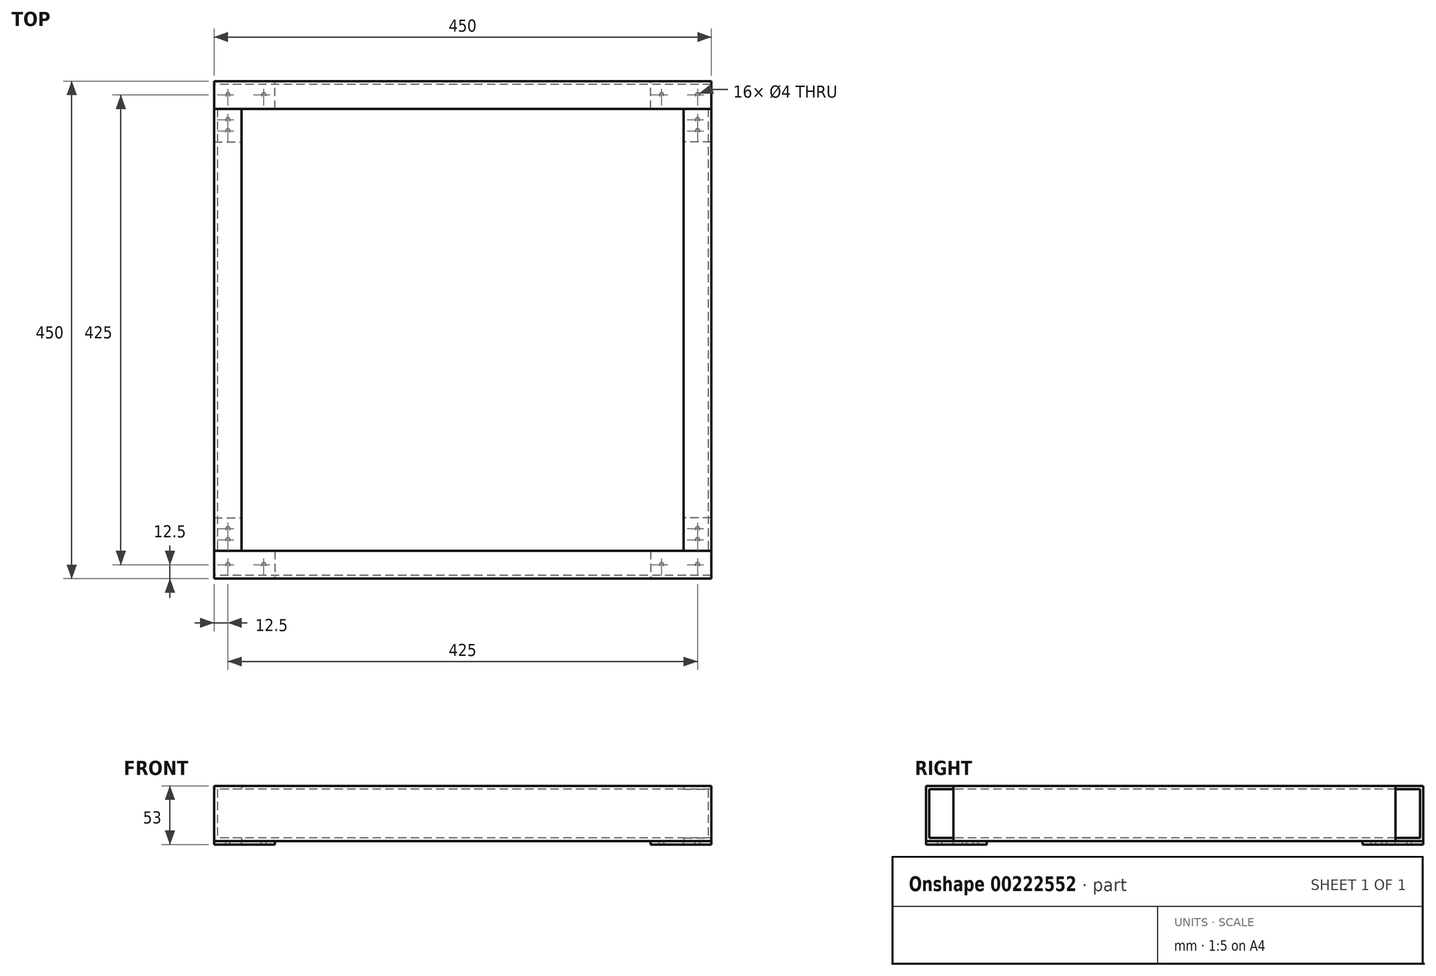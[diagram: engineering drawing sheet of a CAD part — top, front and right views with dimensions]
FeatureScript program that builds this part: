
annotation { "Feature Type Name" : "Feature", "Feature Type Description" : "" }
export const myFeature = defineFeature(function(context is Context, id is Id, definition is map)
    precondition{}
    {
        {
            var Q0;
            Q0=qCreatedBy(makeId("Top.planeOp"),FACE);
            var sketch = newSketch(context, id + "F0", { "sketchPlane" : qUnion([Q0])});
            skLineSegment(sketch, "E0.bottom", {"start": v(225, -225) * mm, "end": v(-225, -225) * mm});
            skLineSegment(sketch, "E0.top", {"start": v(225, 225) * mm, "end": v(-225, 225) * mm});
            skLineSegment(sketch, "E0.left", {"start": v(225, -225) * mm, "end": v(225, 225) * mm});
            skLineSegment(sketch, "E0.right", {"start": v(-225, -225) * mm, "end": v(-225, 225) * mm});
            skPoint(sketch, "E0.middle", {"position": v(0, 0) * mm});
            skLineSegment(sketch, "E1.bottom", {"start": v(200, -200) * mm, "end": v(-200, -200) * mm});
            skLineSegment(sketch, "E1.top", {"start": v(200, 200) * mm, "end": v(-200, 200) * mm});
            skLineSegment(sketch, "E1.left", {"start": v(200, -200) * mm, "end": v(200, 200) * mm});
            skLineSegment(sketch, "E1.right", {"start": v(-200, -200) * mm, "end": v(-200, 200) * mm});
            skLineSegment(sketch, "E2", {"start": v(-200, 200) * mm, "end": v(-225, 200) * mm});
            skLineSegment(sketch, "E3", {"start": v(200, 200) * mm, "end": v(225, 200) * mm});
            skLineSegment(sketch, "E4", {"start": v(-200, -200) * mm, "end": v(-225, -200) * mm});
            skLineSegment(sketch, "E5", {"start": v(200, -200) * mm, "end": v(225, -200) * mm});
            skSolve(sketch);
        }
        {
            var Q0;
            Q0=makeQuery(id+"F0.imprint","IMPRINT",FACE,{"disambiguationData":[TD([[makeQuery(id+"F0.imprint","IMPRINT",EDGE,{"derivedFrom":sQuery(id+"F0.wireOp",EDGE,"E1.right")}),1.0]])]});
            extrude(context, id + "F1", {"entities" : qUnion([Q0]), "depth" : 50 * mm});
        }
        {
            var Q0;
            {var subQ1=sQuery(id+"F0.wireOp",EDGE,"E0.top");Q0=makeQuery(id+"F0.imprint","IMPRINT",FACE,{"disambiguationData":[TD([[makeQuery(id+"F0.imprint","IMPRINT",EDGE,{"derivedFrom":subQ1}),1.0]])]});}
            extrude(context, id + "F2", {"entities" : qUnion([Q0]), "depth" : 50 * mm});
        }
        {
            var Q0;
            Q0=makeQuery(id+"F2.opExtrude","SWEPT_FACE",FACE,{"disambiguationData":[OSD([sQuery(id+"F0.wireOp",EDGE,"E0.right")])]});
            var sketch = newSketch(context, id + "F3", { "sketchPlane" : qUnion([Q0])});
            skLineSegment(sketch, "E6.bottom", {"start": v(-200, 47) * mm, "end": v(-222, 47) * mm});
            skLineSegment(sketch, "E6.top", {"start": v(-200, 3) * mm, "end": v(-222, 3) * mm});
            skLineSegment(sketch, "E6.left", {"start": v(-200, 47) * mm, "end": v(-200, 3) * mm});
            skLineSegment(sketch, "E6.right", {"start": v(-222, 47) * mm, "end": v(-222, 3) * mm});
            skLineSegment(sketch, "E7", {"start": v(-215.1, 47) * mm, "end": v(-215.1, 50) * mm, "construction": true});
            skLineSegment(sketch, "E8", {"start": v(-211, 3) * mm, "end": v(-211, 0) * mm, "construction": true});
            skLineSegment(sketch, "E9", {"start": v(-222, 29.53) * mm, "end": v(-225, 29.53) * mm, "construction": true});
            skSolve(sketch);
        }
        {
            var Q0;
            Q0 = qSketchRegion(id + "F3", true);
            var Q1;
            Q1=makeQuery(id+"F2.opExtrude","SWEPT_FACE",FACE,{"disambiguationData":[OSD([sQuery(id+"F0.wireOp",EDGE,"E0.left")])]});
            extrude(context, id + "F4", {"entities" : qUnion([Q0]), "operationType" : NewBodyOperationType.REMOVE, "endBound" : BoundingType.UP_TO_SURFACE, "oppositeDirection" : true, "endBoundEntityFace" : qUnion([Q1]), "depth" : 25 * mm});
        }
        {
            var Q0;
            Q0=makeQuery(id+"F2.opExtrude","SWEPT_BODY",BODY,{"disambiguationData":[OSD([sQuery(id+"F0.wireOp",EDGE,"E0.top"),sQuery(id+"F0.wireOp",EDGE,"E0.left"),sQuery(id+"F0.wireOp",EDGE,"E0.right"),sQuery(id+"F0.wireOp",EDGE,"E1.top"),sQuery(id+"F0.wireOp",EDGE,"E2"),sQuery(id+"F0.wireOp",EDGE,"E3")])]});
            var Q1;
            Q1=qCreatedBy(makeId("Front.planeOp"),FACE);
            mirror(context, id + "F5", {"entities" : qUnion([Q0]), "mirrorPlane" : qUnion([Q1])});
        }
        {
            var Q0;
            Q0=makeQuery(id+"F1.opExtrude","SWEPT_FACE",FACE,{"disambiguationData":[OSD([sQuery(id+"F0.wireOp",EDGE,"E4")])]});
            var sketch = newSketch(context, id + "F6", { "sketchPlane" : qUnion([Q0])});
            skLineSegment(sketch, "E10.bottom", {"start": v(-200, 47) * mm, "end": v(-222, 47) * mm});
            skLineSegment(sketch, "E10.top", {"start": v(-200, 3) * mm, "end": v(-222, 3) * mm});
            skLineSegment(sketch, "E10.left", {"start": v(-200, 47) * mm, "end": v(-200, 3) * mm});
            skLineSegment(sketch, "E10.right", {"start": v(-222, 47) * mm, "end": v(-222, 3) * mm});
            skLineSegment(sketch, "E11", {"start": v(-211, 47) * mm, "end": v(-211, 50) * mm, "construction": true});
            skLineSegment(sketch, "E12", {"start": v(-222, 25) * mm, "end": v(-225, 25) * mm, "construction": true});
            skLineSegment(sketch, "E13", {"start": v(-211, 3) * mm, "end": v(-211, 0) * mm, "construction": true});
            skPoint(sketch, "E13.endSnap0", {"position": v(-212.5, 0) * mm});
            skSolve(sketch);
        }
        {
            var Q0;
            Q0 = qSketchRegion(id + "F6", true);
            var Q1;
            Q1=makeQuery(id+"F1.opExtrude","SWEPT_FACE",FACE,{"disambiguationData":[OSD([sQuery(id+"F0.wireOp",EDGE,"E2")])]});
            extrude(context, id + "F7", {"entities" : qUnion([Q0]), "operationType" : NewBodyOperationType.REMOVE, "endBound" : BoundingType.UP_TO_SURFACE, "oppositeDirection" : true, "endBoundEntityFace" : qUnion([Q1]), "depth" : 25 * mm});
        }
        {
            var Q0;
            Q0=makeQuery(id+"F1.opExtrude","SWEPT_BODY",BODY,{"disambiguationData":[OSD([sQuery(id+"F0.wireOp",EDGE,"E0.right"),sQuery(id+"F0.wireOp",EDGE,"E1.right"),sQuery(id+"F0.wireOp",EDGE,"E2"),sQuery(id+"F0.wireOp",EDGE,"E4")])]});
            var Q1;
            Q1=qCreatedBy(makeId("Right.planeOp"),FACE);
            mirror(context, id + "F8", {"entities" : qUnion([Q0]), "mirrorPlane" : qUnion([Q1])});
        }
        {
            var Q0;
            Q0=makeQuery(id+"F5.opPattern","COPY",FACE,{"derivedFrom":makeQuery(id+"F2.opExtrude","CAP_FACE",FACE,{"disambiguationData":[OSD([sQuery(id+"F0.wireOp",EDGE,"E0.top"),sQuery(id+"F0.wireOp",EDGE,"E0.left"),sQuery(id+"F0.wireOp",EDGE,"E0.right"),sQuery(id+"F0.wireOp",EDGE,"E1.top"),sQuery(id+"F0.wireOp",EDGE,"E2"),sQuery(id+"F0.wireOp",EDGE,"E3")])],"isStart":true}),"instanceName":"1"});
            var sketch = newSketch(context, id + "F9", { "sketchPlane" : qUnion([Q0])});
            skLineSegment(sketch, "E14", {"start": v(-225, 225) * mm, "end": v(-225, 170) * mm});
            skLineSegment(sketch, "E15", {"start": v(-225, 170) * mm, "end": v(-200, 170) * mm});
            skLineSegment(sketch, "E16", {"start": v(-200, 170) * mm, "end": v(-200, 200) * mm});
            skLineSegment(sketch, "E17", {"start": v(-200, 200) * mm, "end": v(-170, 200) * mm});
            skLineSegment(sketch, "E18", {"start": v(-170, 200) * mm, "end": v(-170, 225) * mm});
            skLineSegment(sketch, "E19", {"start": v(-170, 225) * mm, "end": v(-225, 225) * mm});
            skLineSegment(sketch, "E20", {"start": v(-225, 212.5) * mm, "end": v(-170, 212.5) * mm, "construction": true});
            skLineSegment(sketch, "E21", {"start": v(-212.5, 170) * mm, "end": v(-212.5, 225) * mm, "construction": true});
            skCircle(sketch, "E22", {"center": v(-212.5, 212.5) * mm, "radius": 2 * mm});
            skCircle(sketch, "E23", {"center": v(-180, 212.5) * mm, "radius": 2 * mm});
            skCircle(sketch, "E24", {"center": v(-212.5, 180) * mm, "radius": 2 * mm});
            skCircle(sketch, "E25", {"center": v(-212.5, 190) * mm, "radius": 2 * mm});
            skSolve(sketch);
        }
        {
            var Q0;
            Q0 = qSketchRegion(id + "F9", true);
            extrude(context, id + "F10", {"entities" : qUnion([Q0]), "depth" : 3 * mm});
        }
        {
            var Q0;
            Q0=makeQuery(id+"F10.opExtrude","SWEPT_BODY",BODY,{"disambiguationData":[OSD([sQuery(id+"F9.wireOp",EDGE,"E14"),sQuery(id+"F9.wireOp",EDGE,"E15"),sQuery(id+"F9.wireOp",EDGE,"E16"),sQuery(id+"F9.wireOp",EDGE,"E17"),sQuery(id+"F9.wireOp",EDGE,"E18"),sQuery(id+"F9.wireOp",EDGE,"E19"),sQuery(id+"F9.wireOp",EDGE,"E22"),sQuery(id+"F9.wireOp",EDGE,"E23"),sQuery(id+"F9.wireOp",EDGE,"E24"),sQuery(id+"F9.wireOp",EDGE,"E25")])]});
            var Q1;
            Q1=qCreatedBy(makeId("Front.planeOp"),FACE);
            mirror(context, id + "F11", {"entities" : qUnion([Q0]), "mirrorPlane" : qUnion([Q1])});
        }
        {
            var Q0;
            Q0=makeQuery(id+"F10.opExtrude","SWEPT_BODY",BODY,{"disambiguationData":[OSD([sQuery(id+"F9.wireOp",EDGE,"E14"),sQuery(id+"F9.wireOp",EDGE,"E15"),sQuery(id+"F9.wireOp",EDGE,"E16"),sQuery(id+"F9.wireOp",EDGE,"E17"),sQuery(id+"F9.wireOp",EDGE,"E18"),sQuery(id+"F9.wireOp",EDGE,"E19"),sQuery(id+"F9.wireOp",EDGE,"E22"),sQuery(id+"F9.wireOp",EDGE,"E23"),sQuery(id+"F9.wireOp",EDGE,"E24"),sQuery(id+"F9.wireOp",EDGE,"E25")])]});
            var Q1;
            Q1=makeQuery(id+"F11.opPattern","COPY",BODY,{"derivedFrom":makeQuery(id+"F10.opExtrude","SWEPT_BODY",BODY,{"disambiguationData":[OSD([sQuery(id+"F9.wireOp",EDGE,"E14"),sQuery(id+"F9.wireOp",EDGE,"E15"),sQuery(id+"F9.wireOp",EDGE,"E16"),sQuery(id+"F9.wireOp",EDGE,"E17"),sQuery(id+"F9.wireOp",EDGE,"E18"),sQuery(id+"F9.wireOp",EDGE,"E19"),sQuery(id+"F9.wireOp",EDGE,"E22"),sQuery(id+"F9.wireOp",EDGE,"E23"),sQuery(id+"F9.wireOp",EDGE,"E24"),sQuery(id+"F9.wireOp",EDGE,"E25")])]}),"instanceName":"1"});
            var Q2;
            Q2=qCreatedBy(makeId("Right.planeOp"),FACE);
            mirror(context, id + "F12", {"entities" : qUnion([Q0, Q1]), "mirrorPlane" : qUnion([Q2])});
        }
    });
